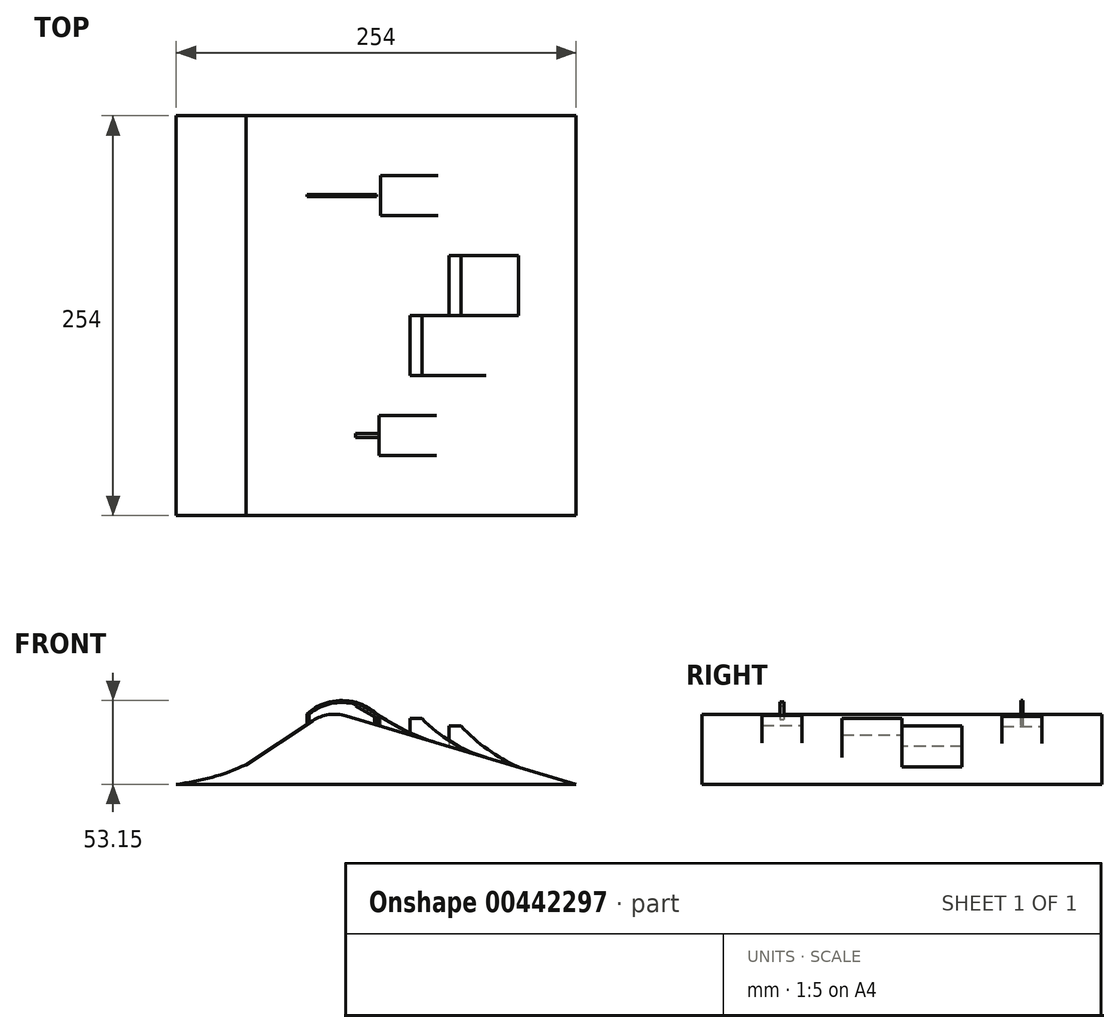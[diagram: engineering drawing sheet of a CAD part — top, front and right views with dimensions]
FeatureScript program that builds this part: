
annotation { "Feature Type Name" : "Feature", "Feature Type Description" : "" }
export const myFeature = defineFeature(function(context is Context, id is Id, definition is map)
    precondition{}
    {
        {
            var Q0;
            Q0=qCreatedBy(makeId("Front.planeOp"),FACE);
            var sketch = newSketch(context, id + "F0", { "sketchPlane" : qUnion([Q0])});
            skLineSegment(sketch, "E0", {"start": v(-56.4, 12.4) * mm, "end": v(-13.94, 40.28) * mm});
            skArc(sketch, "E1", {"start": v(7.23, 43.4) * mm, "mid": v(-3.7, 44.18) * mm, "end": v(-13.94, 40.28) * mm});
            skLineSegment(sketch, "E2", {"start": v(7.23, 43.4) * mm, "end": v(153.32, 0) * mm});
            skLineSegment(sketch, "E3", {"start": v(-75.28, 0) * mm, "end": v(153.32, 0) * mm});
            skArc(sketch, "E4", {"start": v(-100.68, 0) * mm, "mid": v(-78.04, 4.4) * mm, "end": v(-56.4, 12.4) * mm});
            skLineSegment(sketch, "E5", {"start": v(-100.68, 0) * mm, "end": v(-75.28, 0) * mm});
            skSolve(sketch);
        }
        {
            var Q0;
            Q0=makeQuery(id+"F0.imprint","IMPRINT",FACE,{"disambiguationData":[TD([[makeQuery(id+"F0.imprint","IMPRINT",EDGE,{"derivedFrom":sQuery(id+"F0.wireOp",EDGE,"E0")}),-1.0]])]});
            extrude(context, id + "F1", {"entities" : qUnion([Q0]), "endBound" : BoundingType.SYMMETRIC, "depth" : 254 * mm});
        }
        {
            var Q0;
            Q0=qCreatedBy(makeId("Front.planeOp"),FACE);
            var sketch = newSketch(context, id + "F2", { "sketchPlane" : qUnion([Q0])});
            skLineSegment(sketch, "E6", {"start": v(55.39, 29.1) * mm, "end": v(96.12, 17) * mm});
            skArc(sketch, "E7", {"start": v(55.39, 41.8) * mm, "mid": v(74.14, 26.75) * mm, "end": v(96.12, 17) * mm});
            skLineSegment(sketch, "E8.bottom", {"start": v(55.39, 41.8) * mm, "end": v(47.77, 41.8) * mm});
            skLineSegment(sketch, "E8.top", {"start": v(55.39, 29.1) * mm, "end": v(47.77, 29.1) * mm});
            skLineSegment(sketch, "E8.left", {"start": v(55.39, 41.8) * mm, "end": v(55.39, 29.1) * mm});
            skLineSegment(sketch, "E8.right", {"start": v(47.77, 41.8) * mm, "end": v(47.77, 29.1) * mm});
            skSolve(sketch);
        }
        {
            var Q0;
            Q0=makeQuery(id+"F2.imprint","IMPRINT",FACE,{"disambiguationData":[TD([[makeQuery(id+"F2.imprint","IMPRINT",EDGE,{"derivedFrom":sQuery(id+"F2.wireOp",EDGE,"E6")}),1.0]])]});
            var Q1;
            Q1=makeQuery(id+"F2.imprint","IMPRINT",FACE,{"disambiguationData":[TD([[makeQuery(id+"F2.imprint","IMPRINT",EDGE,{"derivedFrom":sQuery(id+"F2.wireOp",EDGE,"E8.bottom")}),1.0]])]});
            extrude(context, id + "F3", {"entities" : qUnion([Q0, Q1]), "operationType" : NewBodyOperationType.ADD, "depth" : 38.1 * mm});
        }
        {
            var Q0;
            Q0=qCreatedBy(makeId("Front.planeOp"),FACE);
            var sketch = newSketch(context, id + "F4", { "sketchPlane" : qUnion([Q0])});
            skArc(sketch, "E9", {"start": v(80.28, 36.94) * mm, "mid": v(97.2, 22.03) * mm, "end": v(116.8, 10.85) * mm});
            skLineSegment(sketch, "E10", {"start": v(116.8, 10.85) * mm, "end": v(80.28, 21.7) * mm});
            skLineSegment(sketch, "E11.bottom", {"start": v(80.28, 36.94) * mm, "end": v(72.66, 36.94) * mm});
            skLineSegment(sketch, "E11.top", {"start": v(80.28, 21.7) * mm, "end": v(72.66, 21.7) * mm});
            skLineSegment(sketch, "E11.left", {"start": v(80.28, 36.94) * mm, "end": v(80.28, 21.7) * mm});
            skLineSegment(sketch, "E11.right", {"start": v(72.66, 36.94) * mm, "end": v(72.66, 21.7) * mm});
            skSolve(sketch);
        }
        {
            var Q0;
            Q0=makeQuery(id+"F4.imprint","IMPRINT",FACE,{"disambiguationData":[TD([[makeQuery(id+"F4.imprint","IMPRINT",EDGE,{"derivedFrom":sQuery(id+"F4.wireOp",EDGE,"E9")}),-1.0]])]});
            var Q1;
            Q1=makeQuery(id+"F4.imprint","IMPRINT",FACE,{"disambiguationData":[TD([[makeQuery(id+"F4.imprint","IMPRINT",EDGE,{"derivedFrom":sQuery(id+"F4.wireOp",EDGE,"E11.bottom")}),1.0]])]});
            extrude(context, id + "F5", {"entities" : qUnion([Q0, Q1]), "operationType" : NewBodyOperationType.ADD, "oppositeDirection" : true, "depth" : 38.1 * mm});
        }
        {
            var Q0;
            Q0=qCreatedBy(makeId("Front.planeOp"),FACE);
            cPlane(context, id + "F6", {"entities" : qUnion([Q0]), "cplaneType" : CPlaneType.OFFSET, "offset" : 76.2 * mm, "width" : 152.4 * mm, "height" : 152.4 * mm});
        }
        {
            var Q0;
            Q0=qCreatedBy(id+"F6.planeOp",FACE);
            var sketch = newSketch(context, id + "F7", { "sketchPlane" : qUnion([Q0])});
            skLineSegment(sketch, "E12", {"start": v(28.05, 37.21) * mm, "end": v(28.05, 43.56) * mm});
            skLineSegment(sketch, "E13", {"start": v(64.57, 26.36) * mm, "end": v(28.05, 37.21) * mm});
            skArc(sketch, "E14", {"start": v(28.05, 43.56) * mm, "mid": v(45.66, 33.58) * mm, "end": v(64.57, 26.36) * mm});
            skSolve(sketch);
        }
        {
            var Q0;
            Q0=makeQuery(id+"F7.imprint","IMPRINT",FACE,{"disambiguationData":[TD([[makeQuery(id+"F7.imprint","IMPRINT",EDGE,{"derivedFrom":sQuery(id+"F7.wireOp",EDGE,"E12")}),-1.0]])]});
            extrude(context, id + "F8", {"entities" : qUnion([Q0]), "operationType" : NewBodyOperationType.ADD, "endBound" : BoundingType.SYMMETRIC, "depth" : 25.4 * mm});
        }
        {
            var Q0;
            Q0=qCreatedBy(makeId("Front.planeOp"),FACE);
            cPlane(context, id + "F9", {"entities" : qUnion([Q0]), "cplaneType" : CPlaneType.OFFSET, "offset" : 76.2 * mm, "oppositeDirection" : true, "width" : 152.4 * mm, "height" : 152.4 * mm});
        }
        {
            var Q0;
            Q0=qCreatedBy(id+"F9.planeOp",FACE);
            var sketch = newSketch(context, id + "F10", { "sketchPlane" : qUnion([Q0])});
            skLineSegment(sketch, "E15", {"start": v(29.2, 43.22) * mm, "end": v(29.2, 36.87) * mm});
            skLineSegment(sketch, "E16", {"start": v(29.2, 36.87) * mm, "end": v(65.73, 26.02) * mm});
            skArc(sketch, "E17", {"start": v(29.2, 43.22) * mm, "mid": v(46.82, 33.24) * mm, "end": v(65.73, 26.02) * mm});
            skSolve(sketch);
        }
        {
            var Q0;
            Q0=makeQuery(id+"F10.imprint","IMPRINT",FACE,{"disambiguationData":[TD([[makeQuery(id+"F10.imprint","IMPRINT",EDGE,{"derivedFrom":sQuery(id+"F10.wireOp",EDGE,"E15")}),1.0]])]});
            extrude(context, id + "F11", {"entities" : qUnion([Q0]), "operationType" : NewBodyOperationType.ADD, "endBound" : BoundingType.SYMMETRIC, "depth" : 25.4 * mm});
        }
        {
            var Q0;
            Q0=qCreatedBy(id+"F6.planeOp",FACE);
            var sketch = newSketch(context, id + "F12", { "sketchPlane" : qUnion([Q0])});
            skLineSegment(sketch, "E18", {"start": v(28.05, 43.56) * mm, "end": v(13.23, 52.12) * mm});
            skLineSegment(sketch, "E19", {"start": v(13.23, 49.58) * mm, "end": v(28.05, 41.02) * mm});
            skLineSegment(sketch, "E20", {"start": v(28.05, 43.56) * mm, "end": v(28.05, 41.02) * mm});
            skLineSegment(sketch, "E21", {"start": v(13.23, 52.12) * mm, "end": v(13.23, 49.58) * mm});
            skSolve(sketch);
        }
        {
            var Q0;
            Q0=makeQuery(id+"F12.imprint","IMPRINT",FACE,{"disambiguationData":[TD([[makeQuery(id+"F12.imprint","IMPRINT",EDGE,{"derivedFrom":sQuery(id+"F12.wireOp",EDGE,"E18")}),1.0]])]});
            extrude(context, id + "F13", {"entities" : qUnion([Q0]), "operationType" : NewBodyOperationType.ADD, "endBound" : BoundingType.SYMMETRIC, "depth" : 2.54 * mm});
        }
        {
            var Q0;
            Q0=qCreatedBy(id+"F9.planeOp",FACE);
            var sketch = newSketch(context, id + "F14", { "sketchPlane" : qUnion([Q0])});
            skLineSegment(sketch, "E22", {"start": v(26.67, 37.62) * mm, "end": v(26.67, 44.6) * mm});
            skArc(sketch, "E23", {"start": v(26.67, 44.6) * mm, "mid": v(4.5, 53.15) * mm, "end": v(-17.66, 44.6) * mm});
            skLineSegment(sketch, "E24", {"start": v(-17.66, 44.6) * mm, "end": v(-17.66, 37.3) * mm});
            skLineSegment(sketch, "E25", {"start": v(25.4, 38.2) * mm, "end": v(25.4, 44.43) * mm});
            skArc(sketch, "E26", {"start": v(25.4, 44.43) * mm, "mid": v(4.5, 51.88) * mm, "end": v(-16.4, 44.43) * mm});
            skLineSegment(sketch, "E27", {"start": v(-16.4, 44.43) * mm, "end": v(-16.4, 38.45) * mm});
            skLineSegment(sketch, "E28", {"start": v(26.67, 37.62) * mm, "end": v(25.4, 38.2) * mm});
            skLineSegment(sketch, "E29", {"start": v(-16.4, 38.45) * mm, "end": v(-17.66, 37.3) * mm});
            skSolve(sketch);
        }
        {
            var Q0;
            Q0=makeQuery(id+"F14.imprint","IMPRINT",FACE,{"disambiguationData":[TD([[makeQuery(id+"F14.imprint","IMPRINT",EDGE,{"derivedFrom":sQuery(id+"F14.wireOp",EDGE,"E22")}),1.0]])]});
            extrude(context, id + "F15", {"entities" : qUnion([Q0]), "endBound" : BoundingType.SYMMETRIC, "depth" : 1.27 * mm});
        }
    });
